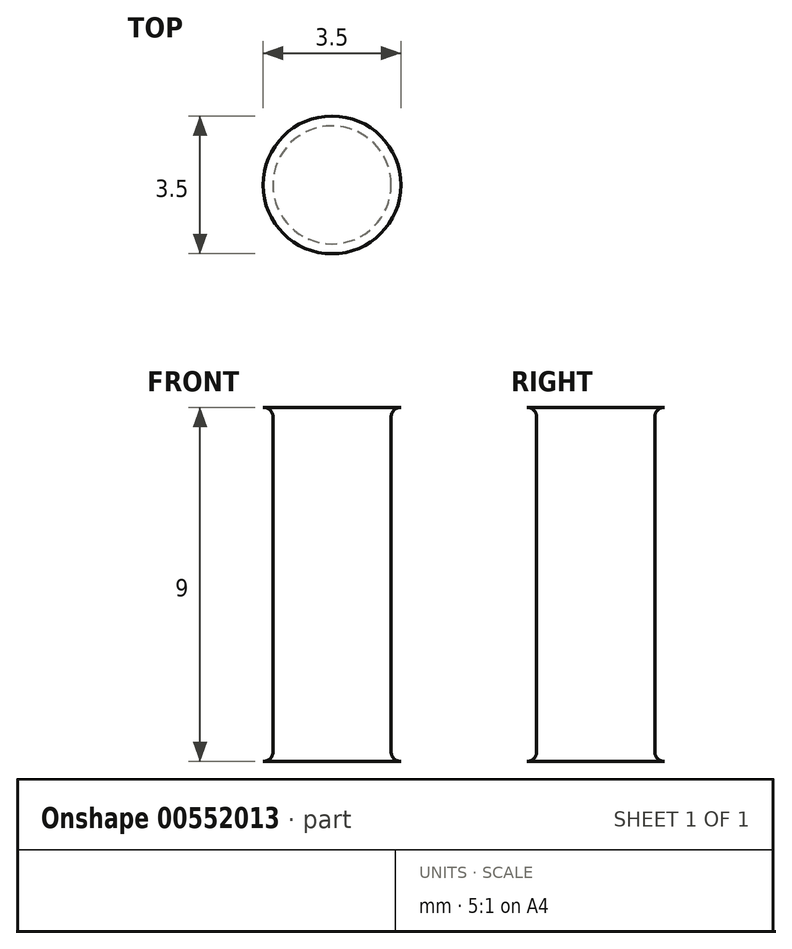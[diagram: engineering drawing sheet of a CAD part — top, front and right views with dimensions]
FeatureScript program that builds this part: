
annotation { "Feature Type Name" : "Feature", "Feature Type Description" : "" }
export const myFeature = defineFeature(function(context is Context, id is Id, definition is map)
    precondition{}
    {
        {
            var Q0;
            Q0=qCreatedBy(makeId("Right.planeOp"),FACE);
            var sketch = newSketch(context, id + "F0", { "sketchPlane" : qUnion([Q0])});
            skLineSegment(sketch, "E0.rect.bottom", {"start": v(-1.75, 4.5) * mm, "end": v(0, 4.5) * mm});
            skLineSegment(sketch, "E0.rect.top", {"start": v(-1.75, -4.5) * mm, "end": v(0, -4.5) * mm});
            skLineSegment(sketch, "E0.rect.left", {"start": v(-1.5, 4.25) * mm, "end": v(-1.5, -4.25) * mm});
            skPoint(sketch, "E0.rect.middle", {"position": v(0, 0) * mm});
            skLineSegment(sketch, "E1", {"start": v(-1.75, 4.5) * mm, "end": v(-1.75, 4.5) * mm});
            skPoint(sketch, "E2.visualSharp", {"position": v(-1.5, 4.5) * mm});
            skArc(sketch, "E2.filletArc", {"start": v(-1.5, 4.25) * mm, "mid": v(-1.57, 4.43) * mm, "end": v(-1.75, 4.5) * mm});
            skLineSegment(sketch, "E3", {"start": v(-1.75, -4.5) * mm, "end": v(-1.75, -4.5) * mm});
            skPoint(sketch, "E4.visualSharp", {"position": v(-1.5, -4.5) * mm});
            skArc(sketch, "E4.filletArc", {"start": v(-1.75, -4.5) * mm, "mid": v(-1.57, -4.43) * mm, "end": v(-1.5, -4.25) * mm});
            skLineSegment(sketch, "E5", {"start": v(0, 4.5) * mm, "end": v(0, -4.5) * mm});
            skSolve(sketch);
        }
        {
            var Q0;
            Q0=qSketchRegion(id+"F0",true);
            var Q1;
            Q1=sQuery(id+"F0.wireOp",EDGE,"E5");
            revolve(context, id + "F1", {"entities" : qUnion([Q0]), "axis" : qUnion([Q1]), "revolveType" : RevolveType.FULL});
        }
    });
